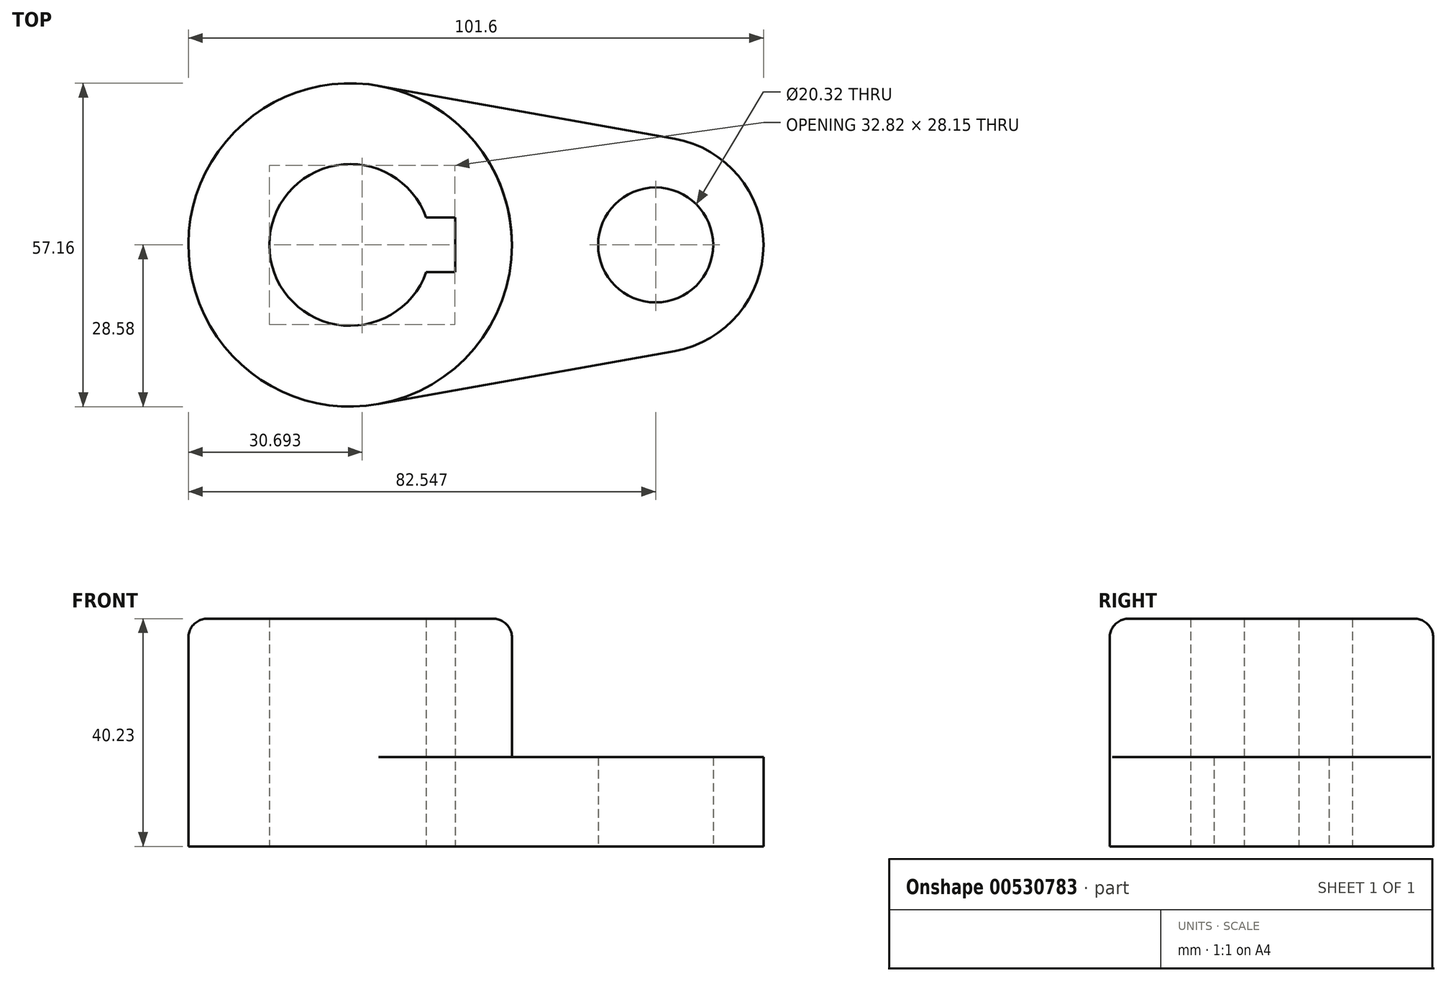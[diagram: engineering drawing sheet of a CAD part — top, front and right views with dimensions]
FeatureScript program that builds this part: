
annotation { "Feature Type Name" : "Feature", "Feature Type Description" : "" }
export const myFeature = defineFeature(function(context is Context, id is Id, definition is map)
    precondition{}
    {
        {
            var Q0;
            Q0=qCreatedBy(makeId("Top.planeOp"),FACE);
            var sketch = newSketch(context, id + "F0", { "sketchPlane" : qUnion([Q0])});
            skCircle(sketch, "E0", {"center": v(26.99, 0) * mm, "radius": 10.16 * mm});
            skArc(sketch, "E1", {"start": v(-21.94, 28.13) * mm, "mid": v(-55.56, 0) * mm, "end": v(-21.94, -28.13) * mm});
            skArc(sketch, "E2", {"start": v(30.35, -18.75) * mm, "mid": v(46.04, 0) * mm, "end": v(30.35, 18.75) * mm});
            skLineSegment(sketch, "E3", {"start": v(-21.94, 28.13) * mm, "end": v(30.35, 18.75) * mm});
            skLineSegment(sketch, "E4", {"start": v(-21.94, -28.13) * mm, "end": v(30.35, -18.75) * mm});
            skSolve(sketch);
        }
        {
            var Q0;
            Q0=qSketchRegion(id+"F0",true);
            extrude(context, id + "F1", {"entities" : qUnion([Q0]), "depth" : 15.77 * mm});
        }
        {
            var Q0;
            Q0=makeQuery(id+"F1.opExtrude","CAP_FACE",FACE,{"disambiguationData":[OSD([sQuery(id+"F0.wireOp",EDGE,"E0"),sQuery(id+"F0.wireOp",EDGE,"E1"),sQuery(id+"F0.wireOp",EDGE,"E2"),sQuery(id+"F0.wireOp",EDGE,"E3"),sQuery(id+"F0.wireOp",EDGE,"E4")])],"isStart":false});
            var sketch = newSketch(context, id + "F2", { "sketchPlane" : qUnion([Q0])});
            skCircle(sketch, "E5", {"center": v(-26.99, 0) * mm, "radius": 28.58 * mm});
            skArc(sketch, "E6", {"start": v(-13.54, 4.83) * mm, "mid": v(-41.27, 0) * mm, "end": v(-13.54, -4.83) * mm});
            skPoint(sketch, "E7", {"position": v(26.99, 0) * mm});
            skLineSegment(sketch, "E8.bottom", {"start": v(-13.54, 4.83) * mm, "end": v(-8.46, 4.83) * mm});
            skLineSegment(sketch, "E8.top", {"start": v(-13.54, -4.83) * mm, "end": v(-8.46, -4.83) * mm});
            skLineSegment(sketch, "E8.right", {"start": v(-8.46, 4.83) * mm, "end": v(-8.46, -4.83) * mm});
            skSolve(sketch);
        }
        {
            var Q0;
            Q0=makeQuery(id+"F2.imprint","IMPRINT",FACE,{"disambiguationData":[TD([[makeQuery(id+"F2.imprint","IMPRINT",EDGE,{"derivedFrom":sQuery(id+"F2.wireOp",EDGE,"E6")}),-1.0]])]});
            extrude(context, id + "F3", {"entities" : qUnion([Q0]), "operationType" : NewBodyOperationType.ADD, "depth" : 24.46 * mm});
        }
        {
            var Q0;
            Q0=makeQuery(id+"F3.opExtrude","CAP_FACE",FACE,{"disambiguationData":[OSD([sQuery(id+"F2.wireOp",EDGE,"E5"),sQuery(id+"F2.wireOp",EDGE,"E6"),sQuery(id+"F2.wireOp",EDGE,"E8.bottom"),sQuery(id+"F2.wireOp",EDGE,"E8.top"),sQuery(id+"F2.wireOp",EDGE,"E8.right")])],"isStart":false});
            var sketch = newSketch(context, id + "F4", { "sketchPlane" : qUnion([Q0])});
            skArc(sketch, "E9.0", {"start": v(-13.54, 4.83) * mm, "mid": v(-41.27, 0) * mm, "end": v(-13.54, -4.83) * mm});
            skLineSegment(sketch, "E9.1", {"start": v(-8.46, 4.83) * mm, "end": v(-8.46, -4.83) * mm});
            skLineSegment(sketch, "E9.2", {"start": v(-13.54, -4.83) * mm, "end": v(-8.46, -4.83) * mm});
            skLineSegment(sketch, "E9.3", {"start": v(-13.54, 4.83) * mm, "end": v(-8.46, 4.83) * mm});
            skSolve(sketch);
        }
        {
            var Q0;
            Q0=qSketchRegion(id+"F4",true);
            extrude(context, id + "F5", {"entities" : qUnion([Q0]), "operationType" : NewBodyOperationType.REMOVE, "endBound" : BoundingType.THROUGH_ALL, "oppositeDirection" : true, "depth" : 25.4 * mm});
        }
        {
            var Q0;
            Q0=makeQuery(id+"F3.opExtrude","CAP_EDGE",EDGE,{"disambiguationData":[OSD([sQuery(id+"F2.wireOp",EDGE,"E5")])],"isStart":false});
            fillet(context, id + "F6", {"entities" : qUnion([Q0]), "radius" : 3.3 * mm, "tangentPropagation" : true, "allowEdgeOverflow" : false});
        }
    });
